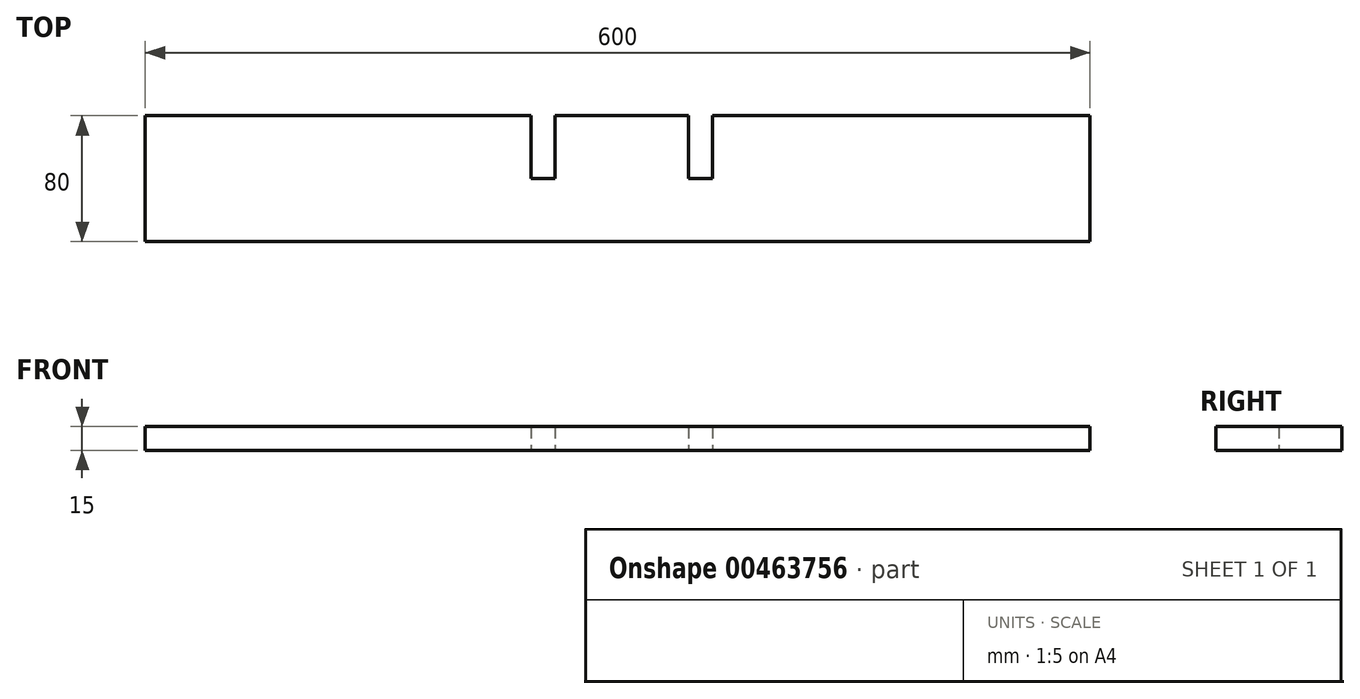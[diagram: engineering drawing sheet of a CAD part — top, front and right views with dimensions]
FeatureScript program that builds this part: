
annotation { "Feature Type Name" : "Feature", "Feature Type Description" : "" }
export const myFeature = defineFeature(function(context is Context, id is Id, definition is map)
    precondition{}
    {
        {
            var Q0;
            Q0=qCreatedBy(makeId("Top.planeOp"),FACE);
            var sketch = newSketch(context, id + "F0", { "sketchPlane" : qUnion([Q0])});
            skLineSegment(sketch, "E0.bottom", {"start": v(-302.66, 78.6) * mm, "end": v(297.34, 78.6) * mm});
            skLineSegment(sketch, "E0.top", {"start": v(-302.66, -1.4) * mm, "end": v(297.34, -1.4) * mm});
            skLineSegment(sketch, "E0.left", {"start": v(-302.66, 78.6) * mm, "end": v(-302.66, -1.4) * mm});
            skLineSegment(sketch, "E0.right", {"start": v(297.34, 78.6) * mm, "end": v(297.34, -1.4) * mm});
            skLineSegment(sketch, "E1.bottom", {"start": v(-57.5, 78.6) * mm, "end": v(-42.5, 78.6) * mm});
            skLineSegment(sketch, "E1.top", {"start": v(-57.5, 38.6) * mm, "end": v(-42.5, 38.6) * mm});
            skLineSegment(sketch, "E1.left", {"start": v(-57.5, 78.6) * mm, "end": v(-57.5, 38.6) * mm});
            skLineSegment(sketch, "E1.right", {"start": v(-42.5, 78.6) * mm, "end": v(-42.5, 38.6) * mm});
            skLineSegment(sketch, "E2.bottom", {"start": v(42.5, 78.6) * mm, "end": v(57.5, 78.6) * mm});
            skLineSegment(sketch, "E2.top", {"start": v(42.5, 38.6) * mm, "end": v(57.5, 38.6) * mm});
            skLineSegment(sketch, "E2.left", {"start": v(42.5, 78.6) * mm, "end": v(42.5, 38.6) * mm});
            skLineSegment(sketch, "E2.right", {"start": v(57.5, 78.6) * mm, "end": v(57.5, 38.6) * mm});
            skSolve(sketch);
        }
        {
            var Q0;
            Q0=makeQuery(id+"F0.imprint","IMPRINT",FACE,{"disambiguationData":[TD([[makeQuery(id+"F0.imprint","IMPRINT",EDGE,{"derivedFrom":sQuery(id+"F0.wireOp",EDGE,"E0.bottom")}),-1.0]])]});
            extrude(context, id + "F1", {"entities" : qUnion([Q0]), "depth" : 15 * mm});
        }
    });
